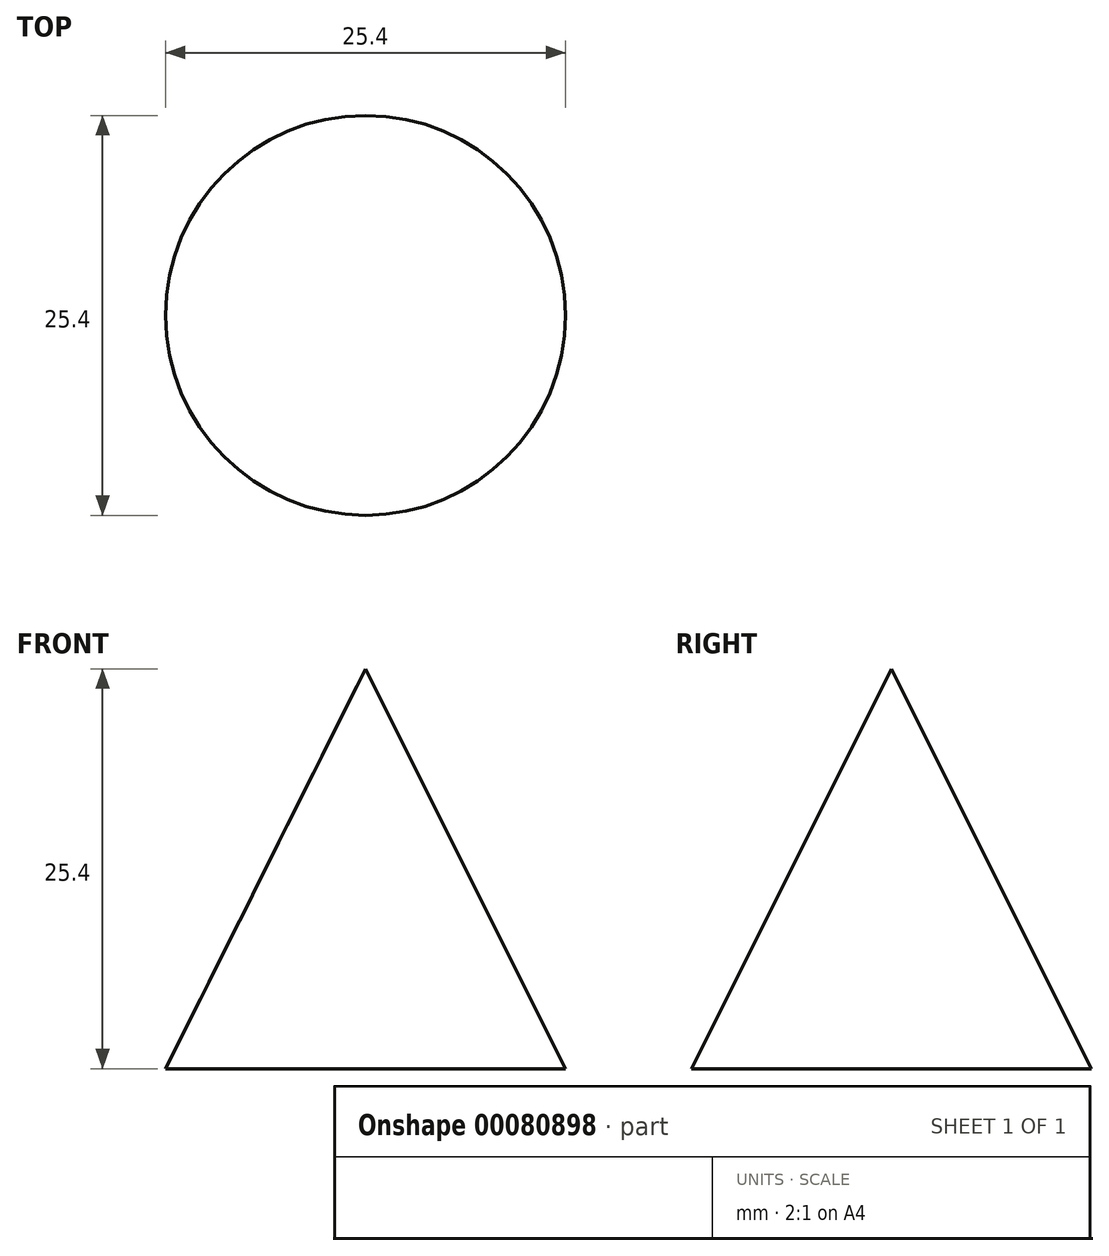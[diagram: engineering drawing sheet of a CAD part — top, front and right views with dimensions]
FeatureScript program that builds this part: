
annotation { "Feature Type Name" : "Feature", "Feature Type Description" : "" }
export const myFeature = defineFeature(function(context is Context, id is Id, definition is map)
    precondition{}
    {
        {
            var Q0;
            Q0=qCreatedBy(makeId("Front.planeOp"),FACE);
            var sketch = newSketch(context, id + "F0", { "sketchPlane" : qUnion([Q0])});
            skLineSegment(sketch, "E0", {"start": v(0, 0) * mm, "end": v(0, 25.4) * mm});
            skLineSegment(sketch, "E1", {"start": v(0, 25.4) * mm, "end": v(12.7, 0) * mm});
            skLineSegment(sketch, "E2", {"start": v(12.7, 0) * mm, "end": v(0, 0) * mm});
            skSolve(sketch);
        }
        {
            var Q0;
            Q0 = qSketchRegion(id + "F0", true);
            var Q1;
            Q1=sQuery(id+"F0.wireOp",EDGE,"E0");
            revolve(context, id + "F1", {"entities" : qUnion([Q0]), "axis" : qUnion([Q1]), "revolveType" : RevolveType.FULL});
        }
    });
